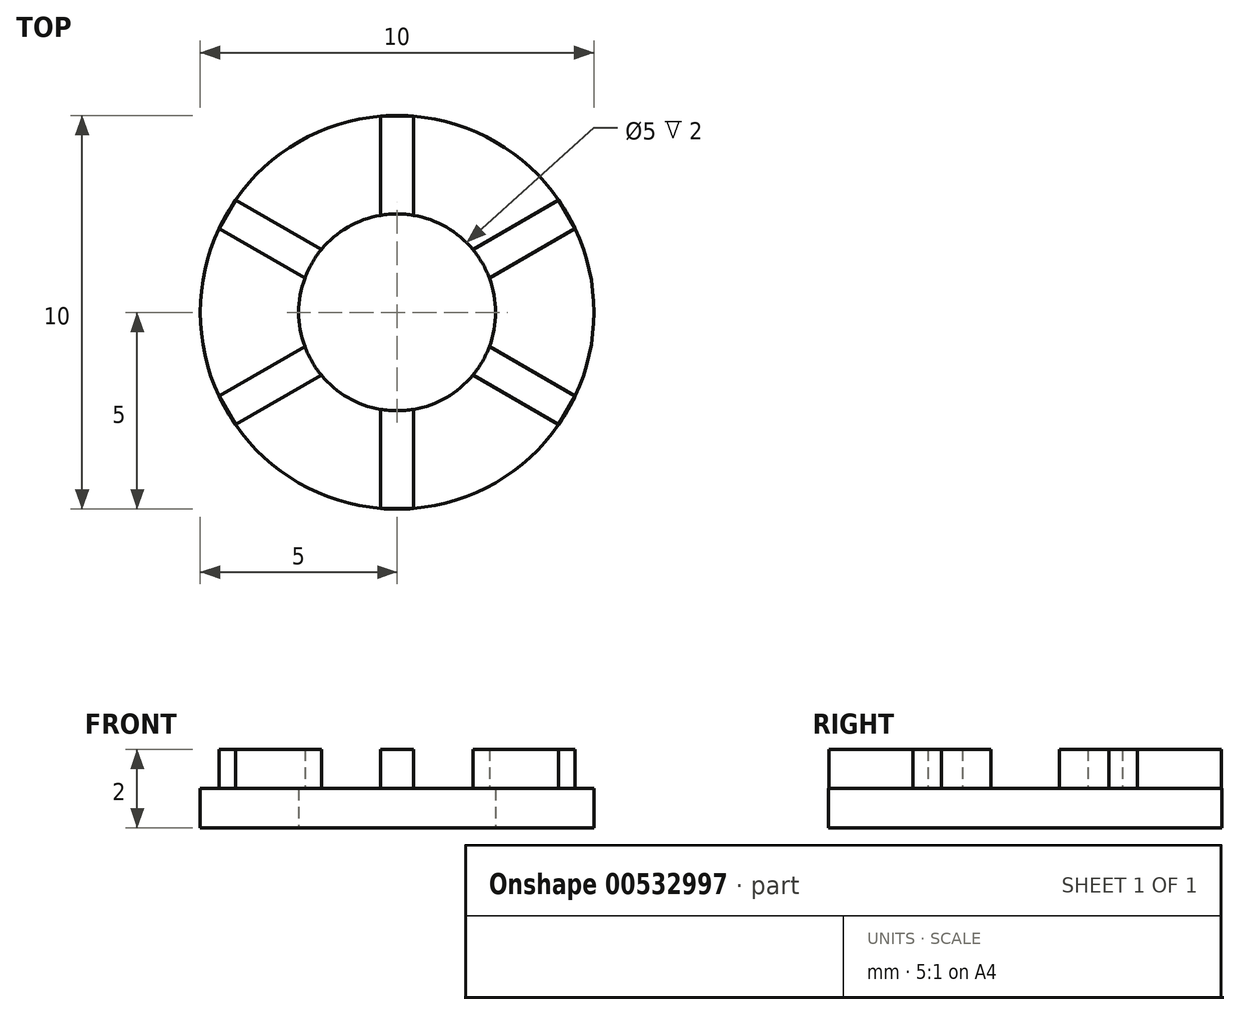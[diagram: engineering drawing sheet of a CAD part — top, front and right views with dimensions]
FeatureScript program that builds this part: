
annotation { "Feature Type Name" : "Feature", "Feature Type Description" : "" }
export const myFeature = defineFeature(function(context is Context, id is Id, definition is map)
    precondition{}
    {
        {
            var Q0;
            Q0=qCreatedBy(makeId("Top.planeOp"),FACE);
            var sketch = newSketch(context, id + "F0", { "sketchPlane" : qUnion([Q0])});
            skCircle(sketch, "E0", {"center": v(0, 0) * mm, "radius": 5 * mm});
            skCircle(sketch, "E1", {"center": v(0, 0) * mm, "radius": 2.5 * mm});
            skSolve(sketch);
        }
        {
            var Q0;
            Q0=makeQuery(id+"F0.imprint","IMPRINT",FACE,{"disambiguationData":[TD([[makeQuery(id+"F0.imprint","IMPRINT",EDGE,{"derivedFrom":sQuery(id+"F0.wireOp",EDGE,"E0")}),1.0]])]});
            extrude(context, id + "F1", {"entities" : qUnion([Q0]), "depth" : 1 * mm, "offsetDistance" : 25 * mm});
        }
        {
            var Q0;
            Q0=makeQuery(id+"F1.opExtrude","CAP_FACE",FACE,{"disambiguationData":[OSD([sQuery(id+"F0.wireOp",EDGE,"E0"),sQuery(id+"F0.wireOp",EDGE,"E1")])],"isStart":false});
            var sketch = newSketch(context, id + "F2", { "sketchPlane" : qUnion([Q0])});
            skLineSegment(sketch, "E2.bottom", {"start": v(0.42, 2.46) * mm, "end": v(-0.42, 2.46) * mm});
            skLineSegment(sketch, "E2.top", {"start": v(0.42, 4.98) * mm, "end": v(-0.42, 4.98) * mm});
            skLineSegment(sketch, "E2.left", {"start": v(0.42, 2.46) * mm, "end": v(0.42, 4.98) * mm});
            skLineSegment(sketch, "E2.right", {"start": v(-0.42, 2.46) * mm, "end": v(-0.42, 4.98) * mm});
            skPoint(sketch, "E2.middle", {"position": v(0, 3.72) * mm});
            skPoint(sketch, "E3.1.0", {"position": v(-3.22, 1.86) * mm});
            skLineSegment(sketch, "E3.1.1", {"start": v(-1.92, 1.6) * mm, "end": v(-2.34, 0.87) * mm});
            skLineSegment(sketch, "E3.1.2", {"start": v(-4.1, 2.85) * mm, "end": v(-4.52, 2.13) * mm});
            skLineSegment(sketch, "E3.1.3", {"start": v(-1.92, 1.6) * mm, "end": v(-4.1, 2.85) * mm});
            skLineSegment(sketch, "E3.1.4", {"start": v(-2.34, 0.87) * mm, "end": v(-4.52, 2.13) * mm});
            skPoint(sketch, "E3.2.0", {"position": v(-3.22, -1.86) * mm});
            skLineSegment(sketch, "E3.2.1", {"start": v(-2.34, -0.87) * mm, "end": v(-1.92, -1.6) * mm});
            skLineSegment(sketch, "E3.2.2", {"start": v(-4.52, -2.13) * mm, "end": v(-4.1, -2.85) * mm});
            skLineSegment(sketch, "E3.2.3", {"start": v(-2.34, -0.87) * mm, "end": v(-4.52, -2.13) * mm});
            skLineSegment(sketch, "E3.2.4", {"start": v(-1.92, -1.6) * mm, "end": v(-4.1, -2.85) * mm});
            skPoint(sketch, "E3.3.0", {"position": v(0, -3.72) * mm});
            skLineSegment(sketch, "E3.3.1", {"start": v(-0.42, -2.46) * mm, "end": v(0.42, -2.46) * mm});
            skLineSegment(sketch, "E3.3.2", {"start": v(-0.42, -4.98) * mm, "end": v(0.42, -4.98) * mm});
            skLineSegment(sketch, "E3.3.3", {"start": v(-0.42, -2.46) * mm, "end": v(-0.42, -4.98) * mm});
            skLineSegment(sketch, "E3.3.4", {"start": v(0.42, -2.46) * mm, "end": v(0.42, -4.98) * mm});
            skPoint(sketch, "E3.4.0", {"position": v(3.22, -1.86) * mm});
            skLineSegment(sketch, "E3.4.1", {"start": v(1.92, -1.6) * mm, "end": v(2.34, -0.87) * mm});
            skLineSegment(sketch, "E3.4.2", {"start": v(4.1, -2.85) * mm, "end": v(4.52, -2.13) * mm});
            skLineSegment(sketch, "E3.4.3", {"start": v(1.92, -1.6) * mm, "end": v(4.1, -2.85) * mm});
            skLineSegment(sketch, "E3.4.4", {"start": v(2.34, -0.87) * mm, "end": v(4.52, -2.13) * mm});
            skPoint(sketch, "E3.5.0", {"position": v(3.22, 1.86) * mm});
            skLineSegment(sketch, "E3.5.1", {"start": v(2.34, 0.87) * mm, "end": v(1.92, 1.6) * mm});
            skLineSegment(sketch, "E3.5.2", {"start": v(4.52, 2.13) * mm, "end": v(4.1, 2.85) * mm});
            skLineSegment(sketch, "E3.5.3", {"start": v(2.34, 0.87) * mm, "end": v(4.52, 2.13) * mm});
            skLineSegment(sketch, "E3.5.4", {"start": v(1.92, 1.6) * mm, "end": v(4.1, 2.85) * mm});
            skPoint(sketch, "E3.center", {"position": v(0, 0) * mm});
            skSolve(sketch);
        }
        {
            var Q0;
            Q0=makeQuery(id+"F2.imprint","IMPRINT",FACE,{"disambiguationData":[TD([[makeQuery(id+"F2.imprint","IMPRINT",EDGE,{"derivedFrom":sQuery(id+"F2.wireOp",EDGE,"E2.top")}),1.0]])]});
            var Q1;
            Q1=makeQuery(id+"F2.imprint","IMPRINT",FACE,{"disambiguationData":[TD([[makeQuery(id+"F2.imprint","IMPRINT",EDGE,{"derivedFrom":sQuery(id+"F2.wireOp",EDGE,"E3.1.2")}),1.0]])]});
            var Q2;
            Q2=makeQuery(id+"F2.imprint","IMPRINT",FACE,{"disambiguationData":[TD([[makeQuery(id+"F2.imprint","IMPRINT",EDGE,{"derivedFrom":sQuery(id+"F2.wireOp",EDGE,"E3.2.2")}),1.0]])]});
            var Q3;
            Q3=makeQuery(id+"F2.imprint","IMPRINT",FACE,{"disambiguationData":[TD([[makeQuery(id+"F2.imprint","IMPRINT",EDGE,{"derivedFrom":sQuery(id+"F2.wireOp",EDGE,"E3.3.2")}),1.0]])]});
            var Q4;
            Q4=makeQuery(id+"F2.imprint","IMPRINT",FACE,{"disambiguationData":[TD([[makeQuery(id+"F2.imprint","IMPRINT",EDGE,{"derivedFrom":sQuery(id+"F2.wireOp",EDGE,"E3.4.2")}),1.0]])]});
            var Q5;
            Q5=makeQuery(id+"F2.imprint","IMPRINT",FACE,{"disambiguationData":[TD([[makeQuery(id+"F2.imprint","IMPRINT",EDGE,{"derivedFrom":sQuery(id+"F2.wireOp",EDGE,"E3.5.2")}),1.0]])]});
            extrude(context, id + "F3", {"entities" : qUnion([Q0, Q1, Q2, Q3, Q4, Q5]), "operationType" : NewBodyOperationType.ADD, "depth" : 1 * mm, "offsetDistance" : 25 * mm});
        }
    });
